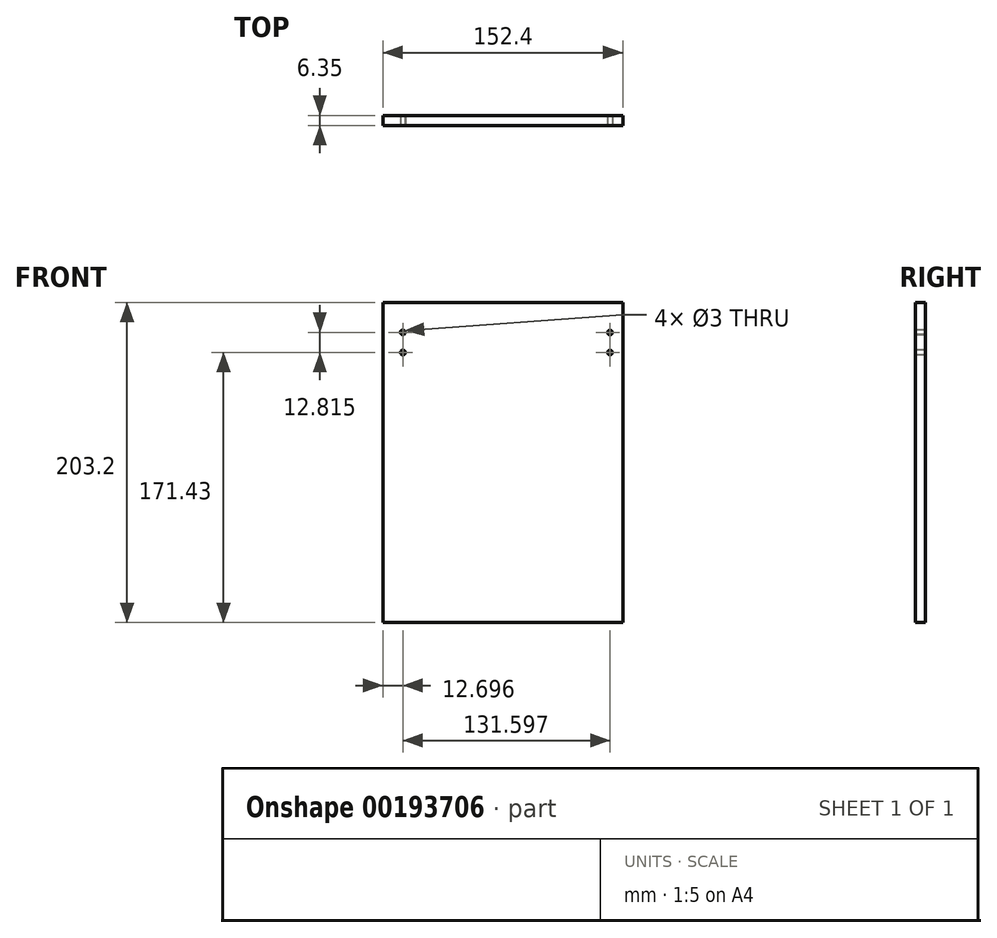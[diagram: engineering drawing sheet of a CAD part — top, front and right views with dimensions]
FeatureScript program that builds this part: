
annotation { "Feature Type Name" : "Feature", "Feature Type Description" : "" }
export const myFeature = defineFeature(function(context is Context, id is Id, definition is map)
    precondition{}
    {
        {
            var Q0;
            Q0=qCreatedBy(makeId("Front.planeOp"),FACE);
            var sketch = newSketch(context, id + "F0", { "sketchPlane" : qUnion([Q0])});
            skLineSegment(sketch, "E0.bottom", {"start": v(76.2, 101.6) * mm, "end": v(-76.2, 101.6) * mm});
            skLineSegment(sketch, "E0.top", {"start": v(76.2, -101.6) * mm, "end": v(-76.2, -101.6) * mm});
            skLineSegment(sketch, "E0.left", {"start": v(76.2, 101.6) * mm, "end": v(76.2, -101.6) * mm});
            skLineSegment(sketch, "E0.right", {"start": v(-76.2, 101.6) * mm, "end": v(-76.2, -101.6) * mm});
            skPoint(sketch, "E0.middle", {"position": v(0, 0) * mm});
            skSolve(sketch);
        }
        {
            var Q0;
            Q0=makeQuery(id+"F0.imprint","IMPRINT",FACE,{"disambiguationData":[TD([[makeQuery(id+"F0.imprint","IMPRINT",EDGE,{"derivedFrom":sQuery(id+"F0.wireOp",EDGE,"E0.bottom")}),1.0]])]});
            extrude(context, id + "F1", {"entities" : qUnion([Q0]), "depth" : 6.35 * mm});
        }
        {
            var Q0;
            Q0=makeQuery(id+"F1.opExtrude","CAP_FACE",FACE,{"disambiguationData":[OSD([sQuery(id+"F0.wireOp",EDGE,"E0.bottom"),sQuery(id+"F0.wireOp",EDGE,"E0.top"),sQuery(id+"F0.wireOp",EDGE,"E0.left"),sQuery(id+"F0.wireOp",EDGE,"E0.right")])],"isStart":false});
            var sketch = newSketch(context, id + "F2", { "sketchPlane" : qUnion([Q0])});
            skLineSegment(sketch, "E1", {"start": v(-63.5, 101.6) * mm, "end": v(-63.5, 82.55) * mm});
            skLineSegment(sketch, "E2", {"start": v(-63.5, 82.55) * mm, "end": v(-63.5, 69.85) * mm});
            skSolve(sketch);
        }
        {
            var Q0;
            Q0=makeQuery(id+"F2.imprint","IMPRINT",FACE,{"disambiguationData":[TD([[makeQuery(id+"F2.imprint","IMPRINT",EDGE,{"derivedFrom":makeQuery(id+"F1.opExtrude","CAP_EDGE",EDGE,{"disambiguationData":[OSD([sQuery(id+"F0.wireOp",EDGE,"E0.top")])],"isStart":false})}),-1.0]])]});
            var sketch = newSketch(context, id + "F3", { "sketchPlane" : qUnion([Q0])});
            skCircle(sketch, "E3", {"center": v(-63.5, 82.65) * mm, "radius": 1.5 * mm});
            skSolve(sketch);
        }
        {
            var Q0;
            Q0=makeQuery(id+"F2.imprint","IMPRINT",FACE,{"disambiguationData":[TD([[makeQuery(id+"F2.imprint","IMPRINT",EDGE,{"derivedFrom":makeQuery(id+"F1.opExtrude","CAP_EDGE",EDGE,{"disambiguationData":[OSD([sQuery(id+"F0.wireOp",EDGE,"E0.top")])],"isStart":false})}),-1.0]])]});
            var sketch = newSketch(context, id + "F4", { "sketchPlane" : qUnion([Q0])});
            skCircle(sketch, "E4", {"center": v(-63.45, 69.83) * mm, "radius": 1.5 * mm});
            skSolve(sketch);
        }
        {
            var Q0;
            Q0 = qSketchRegion(id + "F4", true);
            var Q1;
            Q1 = qSketchRegion(id + "F3", true);
            var Q2;
            Q2=sQuery(id+"F3.wireOp",EDGE,"E3");
            extrude(context, id + "F5", {"entities" : qUnion([Q0, Q1]), "operationType" : NewBodyOperationType.REMOVE, "surfaceEntities" : qUnion([Q2]), "oppositeDirection" : true, "depth" : 159.77 * mm});
        }
        {
            var Q0;
            Q0=makeQuery(id+"F2.imprint","IMPRINT",FACE,{"disambiguationData":[TD([[makeQuery(id+"F2.imprint","IMPRINT",EDGE,{"derivedFrom":makeQuery(id+"F1.opExtrude","CAP_EDGE",EDGE,{"disambiguationData":[OSD([sQuery(id+"F0.wireOp",EDGE,"E0.top")])],"isStart":false})}),-1.0]])]});
            var sketch = newSketch(context, id + "F6", { "sketchPlane" : qUnion([Q0])});
            skCircle(sketch, "E5", {"center": v(68.1, 82.5) * mm, "radius": 1.5 * mm});
            skCircle(sketch, "E6", {"center": v(68.06, 69.86) * mm, "radius": 1.5 * mm});
            skSolve(sketch);
        }
        {
            var Q0;
            Q0 = qSketchRegion(id + "F6", true);
            extrude(context, id + "F7", {"entities" : qUnion([Q0]), "operationType" : NewBodyOperationType.REMOVE, "oppositeDirection" : true, "depth" : 116.84 * mm});
        }
    });
